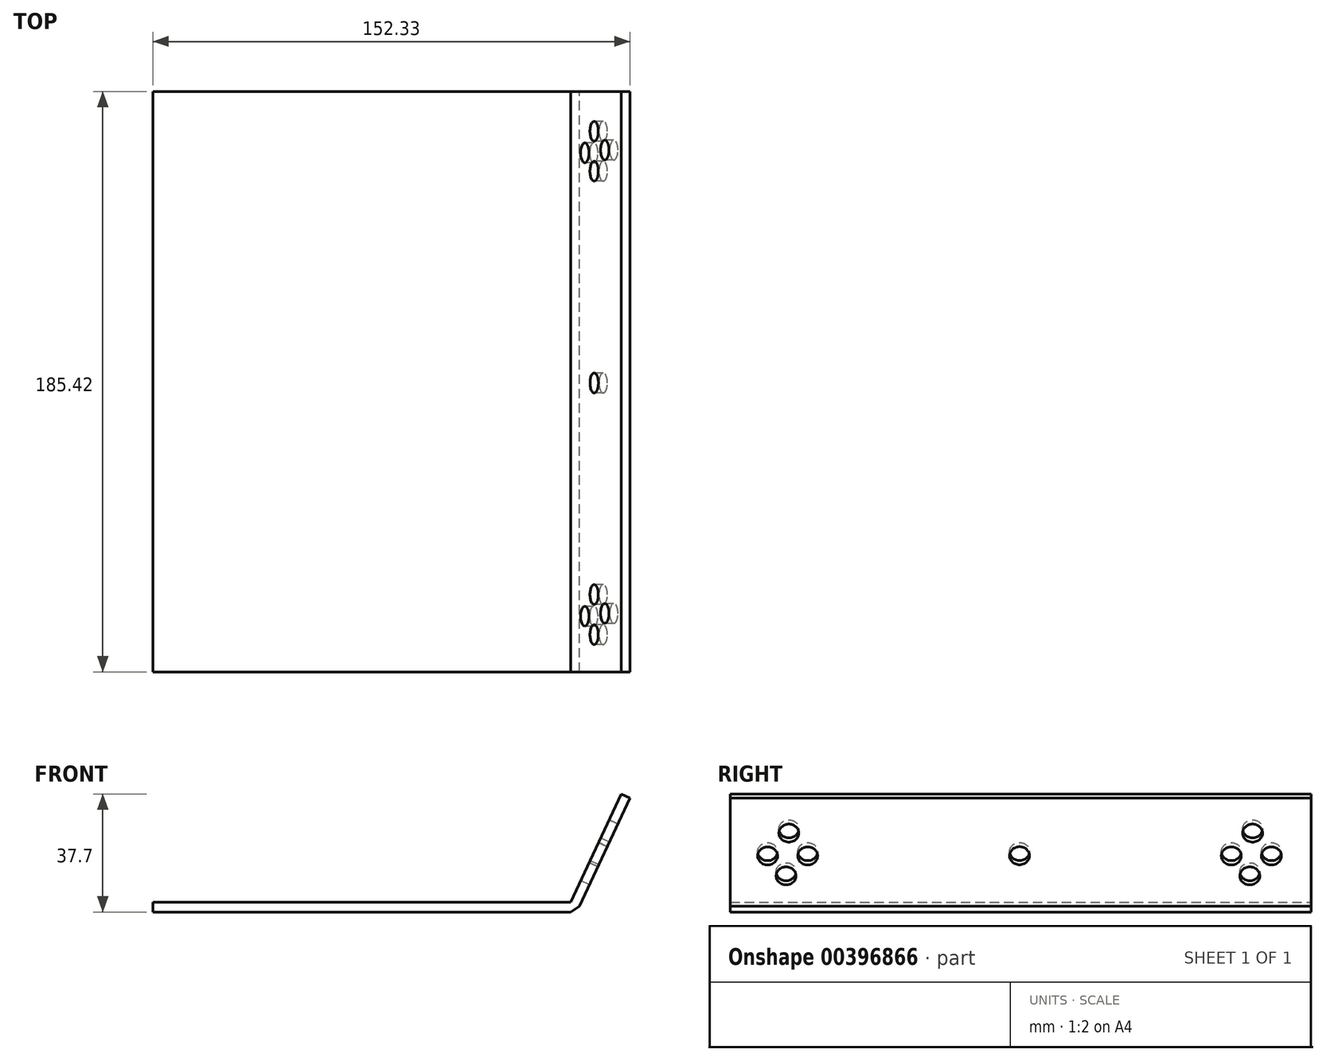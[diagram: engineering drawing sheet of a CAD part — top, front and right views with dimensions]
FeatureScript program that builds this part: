
annotation { "Feature Type Name" : "Feature", "Feature Type Description" : "" }
export const myFeature = defineFeature(function(context is Context, id is Id, definition is map)
    precondition{}
    {
        {
            var Q0;
            Q0=qCreatedBy(makeId("Front.planeOp"),FACE);
            var sketch = newSketch(context, id + "F0", { "sketchPlane" : qUnion([Q0])});
            skLineSegment(sketch, "E0.bottom", {"start": v(-48.41, 17.7) * mm, "end": v(84.94, 17.7) * mm});
            skLineSegment(sketch, "E0.top", {"start": v(-48.41, 14.53) * mm, "end": v(84.94, 14.53) * mm});
            skLineSegment(sketch, "E0.left", {"start": v(-48.41, 17.7) * mm, "end": v(-48.41, 14.53) * mm});
            skLineSegment(sketch, "E1.bottom", {"start": v(84.94, 17.7) * mm, "end": v(101.04, 52.23) * mm});
            skLineSegment(sketch, "E1.top", {"start": v(87.82, 16.36) * mm, "end": v(103.92, 50.9) * mm});
            skLineSegment(sketch, "E1.right", {"start": v(101.04, 52.23) * mm, "end": v(103.92, 50.9) * mm});
            skLineSegment(sketch, "E2", {"start": v(84.94, 14.53) * mm, "end": v(87.82, 16.36) * mm});
            skSolve(sketch);
        }
        {
            var Q0;
            Q0 = qSketchRegion(id + "F0", true);
            extrude(context, id + "F1", {"entities" : qUnion([Q0]), "depth" : 185.42 * mm});
        }
        {
            var Q0;
            Q0=makeQuery(id+"F1.opExtrude","SWEPT_FACE",FACE,{"disambiguationData":[OSD([sQuery(id+"F0.wireOp",EDGE,"E1.bottom")])]});
            var sketch = newSketch(context, id + "F2", { "sketchPlane" : qUnion([Q0])});
            skCircle(sketch, "E3", {"center": v(166.73, 77.74) * mm, "radius": 2.4 * mm});
            skCircle(sketch, "E4", {"center": v(173.51, 69.7) * mm, "radius": 2.4 * mm});
            skCircle(sketch, "E5", {"center": v(160.71, 69.7) * mm, "radius": 2.4 * mm});
            skCircle(sketch, "E6", {"center": v(167.62, 62.65) * mm, "radius": 2.4 * mm});
            skCircle(sketch, "E7", {"center": v(18.71, 77.74) * mm, "radius": 2.4 * mm});
            skCircle(sketch, "E8", {"center": v(25.5, 69.7) * mm, "radius": 2.4 * mm});
            skCircle(sketch, "E9", {"center": v(12.7, 69.7) * mm, "radius": 2.4 * mm});
            skCircle(sketch, "E10", {"center": v(19.6, 62.65) * mm, "radius": 2.4 * mm});
            skCircle(sketch, "E11", {"center": v(93.1, 69.77) * mm, "radius": 2.4 * mm});
            skSolve(sketch);
        }
        {
            var Q0;
            Q0=sQuery(id+"F2.wireOp",VERTEX,"E7.center");
            var Q1;
            Q1=makeQuery(id+"F1.opExtrude","SWEPT_BODY",BODY,{"disambiguationData":[OSD([sQuery(id+"F0.wireOp",EDGE,"E0.bottom"),sQuery(id+"F0.wireOp",EDGE,"E0.top"),sQuery(id+"F0.wireOp",EDGE,"E0.left"),sQuery(id+"F0.wireOp",EDGE,"E1.bottom"),sQuery(id+"F0.wireOp",EDGE,"E1.top"),sQuery(id+"F0.wireOp",EDGE,"E1.right"),sQuery(id+"F0.wireOp",EDGE,"E2")])]});
            hole(context, id + "F3", {"style" : HoleStyle.SIMPLE, "endStyle" : HoleEndStyle.THROUGH, "holeDiameter" : 6.35 * mm, "isTappedThrough" : true, "tappedDepth" : 12.7 * mm, "tapClearance" : 3, "locations" : qUnion([Q0]), "scope" : qUnion([Q1])});
        }
        {
            var Q0;
            Q0=sQuery(id+"F2.wireOp",VERTEX,"E9.center");
            var Q1;
            Q1=makeQuery(id+"F1.opExtrude","SWEPT_BODY",BODY,{"disambiguationData":[OSD([sQuery(id+"F0.wireOp",EDGE,"E0.bottom"),sQuery(id+"F0.wireOp",EDGE,"E0.top"),sQuery(id+"F0.wireOp",EDGE,"E0.left"),sQuery(id+"F0.wireOp",EDGE,"E1.bottom"),sQuery(id+"F0.wireOp",EDGE,"E1.top"),sQuery(id+"F0.wireOp",EDGE,"E1.right"),sQuery(id+"F0.wireOp",EDGE,"E2")])]});
            hole(context, id + "F4", {"style" : HoleStyle.SIMPLE, "endStyle" : HoleEndStyle.THROUGH, "holeDiameter" : 6.35 * mm, "isTappedThrough" : true, "tappedDepth" : 12.7 * mm, "tapClearance" : 3, "locations" : qUnion([Q0]), "scope" : qUnion([Q1])});
        }
        {
            var Q0;
            Q0=sQuery(id+"F2.wireOp",VERTEX,"E10.center");
            var Q1;
            Q1=makeQuery(id+"F1.opExtrude","SWEPT_BODY",BODY,{"disambiguationData":[OSD([sQuery(id+"F0.wireOp",EDGE,"E0.bottom"),sQuery(id+"F0.wireOp",EDGE,"E0.top"),sQuery(id+"F0.wireOp",EDGE,"E0.left"),sQuery(id+"F0.wireOp",EDGE,"E1.bottom"),sQuery(id+"F0.wireOp",EDGE,"E1.top"),sQuery(id+"F0.wireOp",EDGE,"E1.right"),sQuery(id+"F0.wireOp",EDGE,"E2")])]});
            hole(context, id + "F5", {"style" : HoleStyle.SIMPLE, "endStyle" : HoleEndStyle.THROUGH, "holeDiameter" : 6.35 * mm, "isTappedThrough" : true, "tappedDepth" : 12.7 * mm, "tapClearance" : 3, "locations" : qUnion([Q0]), "scope" : qUnion([Q1])});
        }
        {
            var Q0;
            Q0=sQuery(id+"F2.wireOp",VERTEX,"E8.center");
            var Q1;
            Q1=makeQuery(id+"F1.opExtrude","SWEPT_BODY",BODY,{"disambiguationData":[OSD([sQuery(id+"F0.wireOp",EDGE,"E0.bottom"),sQuery(id+"F0.wireOp",EDGE,"E0.top"),sQuery(id+"F0.wireOp",EDGE,"E0.left"),sQuery(id+"F0.wireOp",EDGE,"E1.bottom"),sQuery(id+"F0.wireOp",EDGE,"E1.top"),sQuery(id+"F0.wireOp",EDGE,"E1.right"),sQuery(id+"F0.wireOp",EDGE,"E2")])]});
            hole(context, id + "F6", {"style" : HoleStyle.SIMPLE, "endStyle" : HoleEndStyle.THROUGH, "holeDiameter" : 6.35 * mm, "isTappedThrough" : true, "tappedDepth" : 12.7 * mm, "tapClearance" : 3, "locations" : qUnion([Q0]), "scope" : qUnion([Q1])});
        }
        {
            var Q0;
            Q0=sQuery(id+"F2.wireOp",VERTEX,"E3.center");
            var Q1;
            Q1=makeQuery(id+"F1.opExtrude","SWEPT_BODY",BODY,{"disambiguationData":[OSD([sQuery(id+"F0.wireOp",EDGE,"E0.bottom"),sQuery(id+"F0.wireOp",EDGE,"E0.top"),sQuery(id+"F0.wireOp",EDGE,"E0.left"),sQuery(id+"F0.wireOp",EDGE,"E1.bottom"),sQuery(id+"F0.wireOp",EDGE,"E1.top"),sQuery(id+"F0.wireOp",EDGE,"E1.right"),sQuery(id+"F0.wireOp",EDGE,"E2")])]});
            hole(context, id + "F7", {"style" : HoleStyle.SIMPLE, "endStyle" : HoleEndStyle.THROUGH, "holeDiameter" : 6.35 * mm, "isTappedThrough" : true, "tappedDepth" : 12.7 * mm, "tapClearance" : 3, "locations" : qUnion([Q0]), "scope" : qUnion([Q1])});
        }
        {
            var Q0;
            Q0=sQuery(id+"F2.wireOp",VERTEX,"E5.center");
            var Q1;
            Q1=makeQuery(id+"F1.opExtrude","SWEPT_BODY",BODY,{"disambiguationData":[OSD([sQuery(id+"F0.wireOp",EDGE,"E0.bottom"),sQuery(id+"F0.wireOp",EDGE,"E0.top"),sQuery(id+"F0.wireOp",EDGE,"E0.left"),sQuery(id+"F0.wireOp",EDGE,"E1.bottom"),sQuery(id+"F0.wireOp",EDGE,"E1.top"),sQuery(id+"F0.wireOp",EDGE,"E1.right"),sQuery(id+"F0.wireOp",EDGE,"E2")])]});
            hole(context, id + "F8", {"style" : HoleStyle.SIMPLE, "endStyle" : HoleEndStyle.THROUGH, "holeDiameter" : 6.35 * mm, "isTappedThrough" : true, "tappedDepth" : 12.7 * mm, "tapClearance" : 3, "locations" : qUnion([Q0]), "scope" : qUnion([Q1])});
        }
        {
            var Q0;
            Q0=sQuery(id+"F2.wireOp",VERTEX,"E6.center");
            var Q1;
            Q1=makeQuery(id+"F1.opExtrude","SWEPT_BODY",BODY,{"disambiguationData":[OSD([sQuery(id+"F0.wireOp",EDGE,"E0.bottom"),sQuery(id+"F0.wireOp",EDGE,"E0.top"),sQuery(id+"F0.wireOp",EDGE,"E0.left"),sQuery(id+"F0.wireOp",EDGE,"E1.bottom"),sQuery(id+"F0.wireOp",EDGE,"E1.top"),sQuery(id+"F0.wireOp",EDGE,"E1.right"),sQuery(id+"F0.wireOp",EDGE,"E2")])]});
            hole(context, id + "F9", {"style" : HoleStyle.SIMPLE, "endStyle" : HoleEndStyle.THROUGH, "holeDiameter" : 6.35 * mm, "isTappedThrough" : true, "tappedDepth" : 12.7 * mm, "tapClearance" : 3, "locations" : qUnion([Q0]), "scope" : qUnion([Q1])});
        }
        {
            var Q0;
            Q0=sQuery(id+"F2.wireOp",VERTEX,"E4.center");
            var Q1;
            Q1=makeQuery(id+"F1.opExtrude","SWEPT_BODY",BODY,{"disambiguationData":[OSD([sQuery(id+"F0.wireOp",EDGE,"E0.bottom"),sQuery(id+"F0.wireOp",EDGE,"E0.top"),sQuery(id+"F0.wireOp",EDGE,"E0.left"),sQuery(id+"F0.wireOp",EDGE,"E1.bottom"),sQuery(id+"F0.wireOp",EDGE,"E1.top"),sQuery(id+"F0.wireOp",EDGE,"E1.right"),sQuery(id+"F0.wireOp",EDGE,"E2")])]});
            hole(context, id + "F10", {"style" : HoleStyle.SIMPLE, "endStyle" : HoleEndStyle.THROUGH, "holeDiameter" : 6.35 * mm, "isTappedThrough" : true, "tappedDepth" : 12.7 * mm, "tapClearance" : 3, "locations" : qUnion([Q0]), "scope" : qUnion([Q1])});
        }
        {
            var Q0;
            Q0=sQuery(id+"F2.wireOp",VERTEX,"E11.center");
            var Q1;
            Q1=makeQuery(id+"F1.opExtrude","SWEPT_BODY",BODY,{"disambiguationData":[OSD([sQuery(id+"F0.wireOp",EDGE,"E0.bottom"),sQuery(id+"F0.wireOp",EDGE,"E0.top"),sQuery(id+"F0.wireOp",EDGE,"E0.left"),sQuery(id+"F0.wireOp",EDGE,"E1.bottom"),sQuery(id+"F0.wireOp",EDGE,"E1.top"),sQuery(id+"F0.wireOp",EDGE,"E1.right"),sQuery(id+"F0.wireOp",EDGE,"E2")])]});
            hole(context, id + "F11", {"style" : HoleStyle.SIMPLE, "endStyle" : HoleEndStyle.THROUGH, "holeDiameter" : 6.35 * mm, "isTappedThrough" : true, "tappedDepth" : 12.7 * mm, "tapClearance" : 3, "locations" : qUnion([Q0]), "scope" : qUnion([Q1])});
        }
    });
